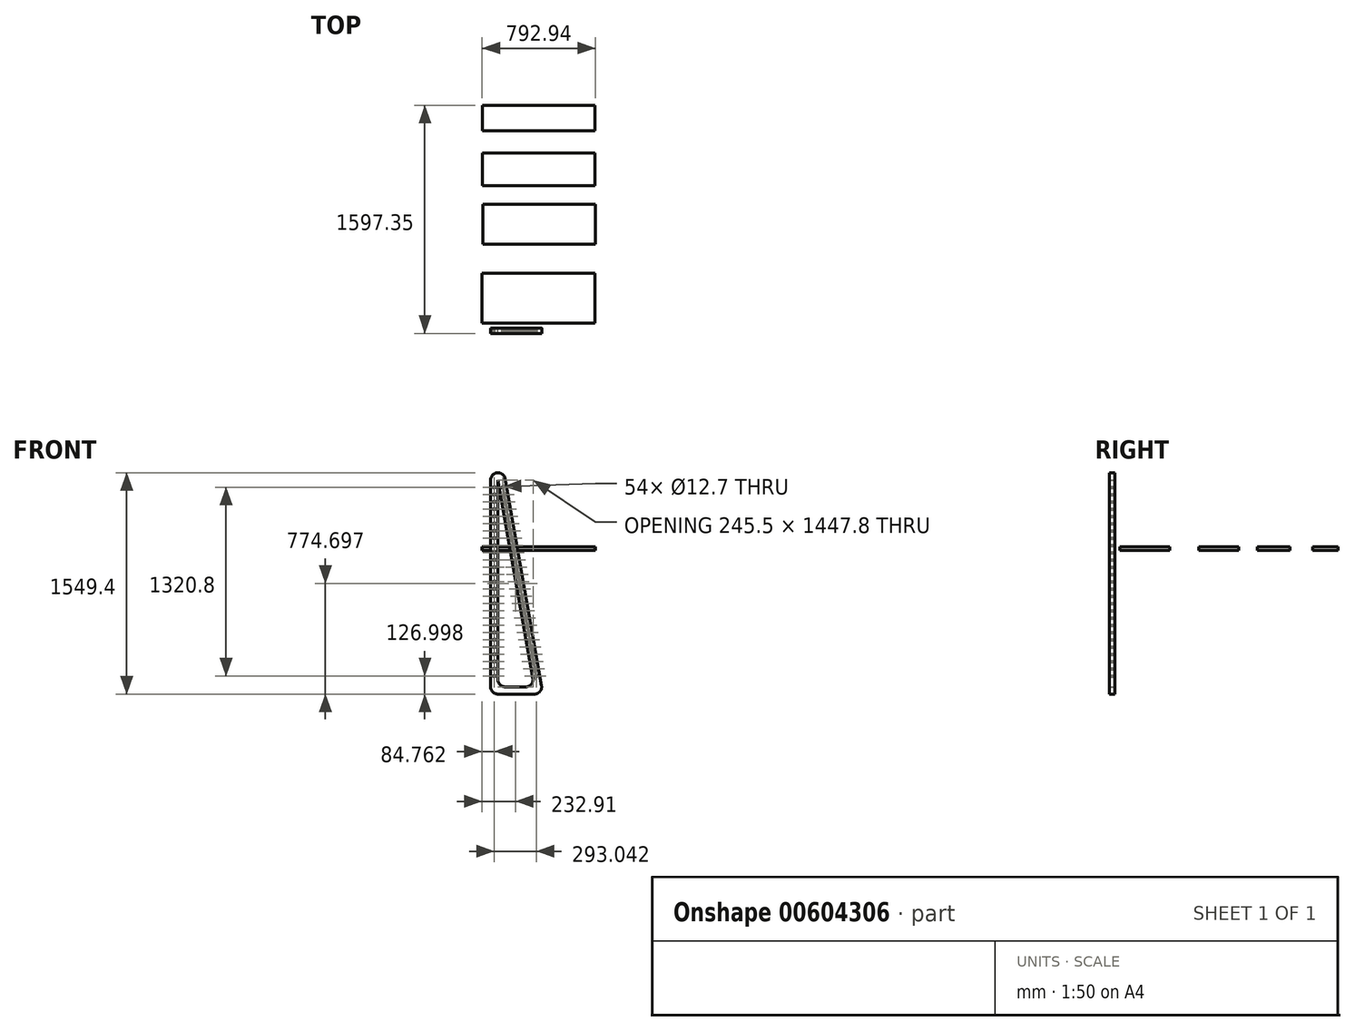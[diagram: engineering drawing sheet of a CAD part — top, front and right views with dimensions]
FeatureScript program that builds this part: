
annotation { "Feature Type Name" : "Feature", "Feature Type Description" : "" }
export const myFeature = defineFeature(function(context is Context, id is Id, definition is map)
    precondition{}
    {
        {
            var Q0;
            Q0=qCreatedBy(makeId("Front.planeOp"),FACE);
            var sketch = newSketch(context, id + "F0", { "sketchPlane" : qUnion([Q0])});
            skLineSegment(sketch, "E0", {"start": v(-166.82, 494.38) * mm, "end": v(-166.82, -902.62) * mm});
            skLineSegment(sketch, "E1", {"start": v(-116.02, -953.42) * mm, "end": v(27.93, -953.42) * mm});
            skLineSegment(sketch, "E2", {"start": v(77.96, -893.8) * mm, "end": v(-166.82, 494.38) * mm});
            skLineSegment(sketch, "E3", {"start": v(-217.62, 494.38) * mm, "end": v(-217.62, -953.42) * mm});
            skLineSegment(sketch, "E4", {"start": v(-166.82, -1004.22) * mm, "end": v(88.47, -1004.22) * mm});
            skLineSegment(sketch, "E5", {"start": v(138.5, -944.6) * mm, "end": v(-116.8, 503.2) * mm});
            skLineSegment(sketch, "E6", {"start": v(-440.16, 1075.02) * mm, "end": v(-440.16, -986.32) * mm, "construction": true});
            skPoint(sketch, "E7.visualSharp", {"position": v(-217.62, 1075.02) * mm});
            skArc(sketch, "E7.filletArc", {"start": v(-116.8, 503.2) * mm, "mid": v(-171.25, 544.98) * mm, "end": v(-217.62, 494.38) * mm});
            skPoint(sketch, "E8.visualSharp", {"position": v(-217.62, -1004.22) * mm});
            skArc(sketch, "E8.filletArc", {"start": v(-217.62, -953.42) * mm, "mid": v(-202.74, -989.34) * mm, "end": v(-166.82, -1004.22) * mm});
            skPoint(sketch, "E9.visualSharp", {"position": v(149, -1004.22) * mm});
            skArc(sketch, "E9.filletArc", {"start": v(88.47, -1004.22) * mm, "mid": v(127.38, -986.08) * mm, "end": v(138.5, -944.6) * mm});
            skArc(sketch, "E10.filletArc", {"start": v(27.93, -953.42) * mm, "mid": v(66.84, -935.28) * mm, "end": v(77.96, -893.8) * mm});
            skArc(sketch, "E11.filletArc", {"start": v(-166.82, -902.62) * mm, "mid": v(-151.94, -938.54) * mm, "end": v(-116.02, -953.42) * mm});
            skLineSegment(sketch, "E12", {"start": v(-166.82, -877.22) * mm, "end": v(-192.22, -877.22) * mm, "construction": true});
            skLineSegment(sketch, "E13", {"start": v(-192.22, -877.22) * mm, "end": v(-217.62, -877.22) * mm, "construction": true});
            skCircle(sketch, "E14", {"center": v(-192.22, -877.22) * mm, "radius": 6.35 * mm});
            skCircle(sketch, "E15.0.1.0", {"center": v(-192.22, -826.42) * mm, "radius": 6.35 * mm});
            skCircle(sketch, "E15.0.2.0", {"center": v(-192.22, -775.62) * mm, "radius": 6.35 * mm});
            skCircle(sketch, "E15.0.3.0", {"center": v(-192.22, -724.82) * mm, "radius": 6.35 * mm});
            skCircle(sketch, "E15.0.4.0", {"center": v(-192.22, -674.02) * mm, "radius": 6.35 * mm});
            skCircle(sketch, "E15.0.5.0", {"center": v(-192.22, -623.22) * mm, "radius": 6.35 * mm});
            skCircle(sketch, "E15.0.6.0", {"center": v(-192.22, -572.42) * mm, "radius": 6.35 * mm});
            skCircle(sketch, "E15.0.7.0", {"center": v(-192.22, -521.62) * mm, "radius": 6.35 * mm});
            skCircle(sketch, "E15.0.8.0", {"center": v(-192.22, -470.82) * mm, "radius": 6.35 * mm});
            skCircle(sketch, "E15.0.9.0", {"center": v(-192.22, -420.02) * mm, "radius": 6.35 * mm});
            skCircle(sketch, "E15.0.10.0", {"center": v(-192.22, -369.22) * mm, "radius": 6.35 * mm});
            skCircle(sketch, "E15.0.11.0", {"center": v(-192.22, -318.42) * mm, "radius": 6.35 * mm});
            skCircle(sketch, "E15.0.12.0", {"center": v(-192.22, -267.62) * mm, "radius": 6.35 * mm});
            skCircle(sketch, "E15.0.13.0", {"center": v(-192.22, -216.82) * mm, "radius": 6.35 * mm});
            skCircle(sketch, "E15.0.14.0", {"center": v(-192.22, -166.02) * mm, "radius": 6.35 * mm});
            skCircle(sketch, "E15.0.15.0", {"center": v(-192.22, -115.22) * mm, "radius": 6.35 * mm});
            skCircle(sketch, "E15.0.16.0", {"center": v(-192.22, -64.42) * mm, "radius": 6.35 * mm});
            skCircle(sketch, "E15.0.17.0", {"center": v(-192.22, -13.62) * mm, "radius": 6.35 * mm});
            skCircle(sketch, "E15.0.18.0", {"center": v(-192.22, 37.18) * mm, "radius": 6.35 * mm});
            skCircle(sketch, "E15.0.19.0", {"center": v(-192.22, 87.98) * mm, "radius": 6.35 * mm});
            skCircle(sketch, "E15.0.20.0", {"center": v(-192.22, 138.78) * mm, "radius": 6.35 * mm});
            skCircle(sketch, "E15.0.21.0", {"center": v(-192.22, 189.58) * mm, "radius": 6.35 * mm});
            skCircle(sketch, "E15.0.22.0", {"center": v(-192.22, 240.38) * mm, "radius": 6.35 * mm});
            skCircle(sketch, "E15.0.23.0", {"center": v(-192.22, 291.18) * mm, "radius": 6.35 * mm});
            skCircle(sketch, "E15.0.24.0", {"center": v(-192.22, 341.98) * mm, "radius": 6.35 * mm});
            skLineSegment(sketch, "E15.direction1", {"start": v(-192.22, -877.22) * mm, "end": v(-134.26, -877.22) * mm, "construction": true});
            skLineSegment(sketch, "E15.direction2", {"start": v(-192.22, -877.22) * mm, "end": v(-192.22, -826.42) * mm, "construction": true});
            skCircle(sketch, "E16.0.0.25", {"center": v(-192.22, 392.78) * mm, "radius": 6.35 * mm});
            skCircle(sketch, "E16.0.0.26", {"center": v(-192.22, 443.58) * mm, "radius": 6.35 * mm});
            skLineSegment(sketch, "E17", {"start": v(101.78, -882.67) * mm, "end": v(-141.8, 498.79) * mm, "construction": true});
            skLineSegment(sketch, "E18", {"start": v(-141.8, 498.79) * mm, "end": v(-116.8, 503.2) * mm, "construction": true});
            skLineSegment(sketch, "E19", {"start": v(-141.8, 498.79) * mm, "end": v(-166.82, 494.38) * mm, "construction": true});
            skLineSegment(sketch, "E20", {"start": v(72.8, -864.58) * mm, "end": v(97.82, -860.17) * mm, "construction": true});
            skLineSegment(sketch, "E21", {"start": v(97.82, -860.17) * mm, "end": v(122.83, -855.76) * mm, "construction": true});
            skCircle(sketch, "E22", {"center": v(100.82, -877.22) * mm, "radius": 6.35 * mm});
            skCircle(sketch, "E23", {"center": v(91.87, -826.42) * mm, "radius": 6.35 * mm});
            skCircle(sketch, "E24", {"center": v(82.9, -775.62) * mm, "radius": 6.35 * mm});
            skCircle(sketch, "E25", {"center": v(73.95, -724.82) * mm, "radius": 6.35 * mm});
            skCircle(sketch, "E26", {"center": v(65, -674.02) * mm, "radius": 6.35 * mm});
            skCircle(sketch, "E27", {"center": v(56.04, -623.22) * mm, "radius": 6.35 * mm});
            skCircle(sketch, "E28", {"center": v(47.08, -572.42) * mm, "radius": 6.35 * mm});
            skCircle(sketch, "E29", {"center": v(38.12, -521.62) * mm, "radius": 6.35 * mm});
            skCircle(sketch, "E30", {"center": v(29.16, -470.82) * mm, "radius": 6.35 * mm});
            skCircle(sketch, "E31", {"center": v(20.2, -420.02) * mm, "radius": 6.35 * mm});
            skCircle(sketch, "E32", {"center": v(11.25, -369.22) * mm, "radius": 6.35 * mm});
            skCircle(sketch, "E33", {"center": v(2.3, -318.42) * mm, "radius": 6.35 * mm});
            skCircle(sketch, "E34", {"center": v(-6.67, -267.62) * mm, "radius": 6.35 * mm});
            skCircle(sketch, "E35", {"center": v(-15.62, -216.82) * mm, "radius": 6.35 * mm});
            skCircle(sketch, "E36", {"center": v(-24.58, -166.02) * mm, "radius": 6.35 * mm});
            skCircle(sketch, "E37", {"center": v(-33.54, -115.22) * mm, "radius": 6.35 * mm});
            skCircle(sketch, "E38", {"center": v(-42.5, -64.42) * mm, "radius": 6.35 * mm});
            skCircle(sketch, "E39", {"center": v(-60.4, 37.18) * mm, "radius": 6.35 * mm});
            skCircle(sketch, "E40", {"center": v(-69.37, 87.98) * mm, "radius": 6.35 * mm});
            skCircle(sketch, "E41", {"center": v(-51.45, -13.62) * mm, "radius": 6.35 * mm});
            skCircle(sketch, "E42", {"center": v(-78.32, 138.78) * mm, "radius": 6.35 * mm});
            skCircle(sketch, "E43", {"center": v(-87.28, 189.58) * mm, "radius": 6.35 * mm});
            skCircle(sketch, "E44", {"center": v(-96.24, 240.38) * mm, "radius": 6.35 * mm});
            skCircle(sketch, "E45", {"center": v(-105.2, 291.18) * mm, "radius": 6.35 * mm});
            skCircle(sketch, "E46", {"center": v(-114.15, 341.98) * mm, "radius": 6.35 * mm});
            skCircle(sketch, "E47", {"center": v(-123.11, 392.78) * mm, "radius": 6.35 * mm});
            skCircle(sketch, "E48", {"center": v(-132.07, 443.58) * mm, "radius": 6.35 * mm});
            skSolve(sketch);
        }
        {
            var Q0;
            Q0 = qSketchRegion(id + "F0", true);
            extrude(context, id + "F1", {"entities" : qUnion([Q0]), "depth" : 38.1 * mm, "offsetDistance" : 25.4 * mm});
        }
        {
            var Q0;
            Q0=qCreatedBy(makeId("Top.planeOp"),FACE);
            var sketch = newSketch(context, id + "F2", { "sketchPlane" : qUnion([Q0])});
            skLineSegment(sketch, "E49.bottom", {"start": v(-276.98, 381.93) * mm, "end": v(510.42, 381.93) * mm});
            skLineSegment(sketch, "E49.top", {"start": v(-276.98, 32.68) * mm, "end": v(510.42, 32.68) * mm});
            skLineSegment(sketch, "E49.left", {"start": v(-276.98, 381.93) * mm, "end": v(-276.98, 32.68) * mm});
            skLineSegment(sketch, "E49.right", {"start": v(510.42, 381.93) * mm, "end": v(510.42, 32.68) * mm});
            skLineSegment(sketch, "E50.bottom", {"start": v(-271.44, 864.31) * mm, "end": v(515.96, 864.31) * mm});
            skLineSegment(sketch, "E50.top", {"start": v(-271.44, 584.91) * mm, "end": v(515.96, 584.91) * mm});
            skLineSegment(sketch, "E50.left", {"start": v(-271.44, 864.31) * mm, "end": v(-271.44, 584.91) * mm});
            skLineSegment(sketch, "E50.right", {"start": v(515.96, 864.31) * mm, "end": v(515.96, 584.91) * mm});
            skLineSegment(sketch, "E51.bottom", {"start": v(-275.9, 995.66) * mm, "end": v(511.5, 995.66) * mm});
            skLineSegment(sketch, "E51.top", {"start": v(-275.9, 1224.26) * mm, "end": v(511.5, 1224.26) * mm});
            skLineSegment(sketch, "E51.left", {"start": v(-275.9, 995.66) * mm, "end": v(-275.9, 1224.26) * mm});
            skLineSegment(sketch, "E51.right", {"start": v(511.5, 995.66) * mm, "end": v(511.5, 1224.26) * mm});
            skLineSegment(sketch, "E52.bottom", {"start": v(-274.18, 1381.45) * mm, "end": v(513.22, 1381.45) * mm});
            skLineSegment(sketch, "E52.top", {"start": v(-274.18, 1559.25) * mm, "end": v(513.22, 1559.25) * mm});
            skLineSegment(sketch, "E52.left", {"start": v(-274.18, 1381.45) * mm, "end": v(-274.18, 1559.25) * mm});
            skLineSegment(sketch, "E52.right", {"start": v(513.22, 1381.45) * mm, "end": v(513.22, 1559.25) * mm});
            skSolve(sketch);
        }
        {
            var Q0;
            Q0 = qSketchRegion(id + "F2", true);
            extrude(context, id + "F3", {"entities" : qUnion([Q0]), "depth" : 25.4 * mm, "offsetDistance" : 25.4 * mm});
        }
    });
